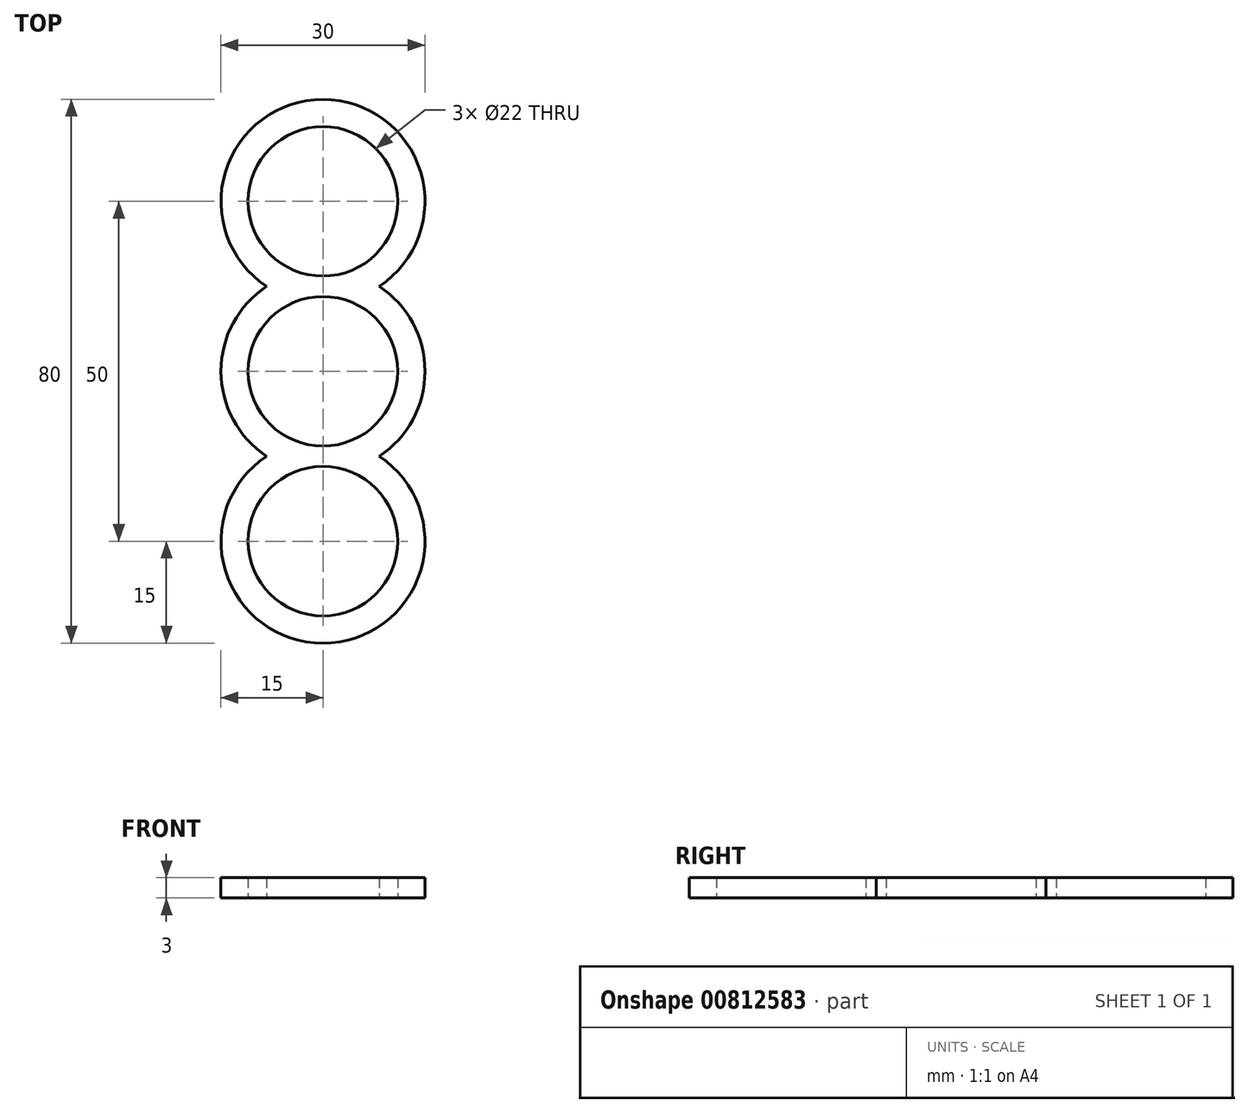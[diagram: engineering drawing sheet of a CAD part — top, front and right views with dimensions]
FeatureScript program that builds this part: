
annotation { "Feature Type Name" : "Feature", "Feature Type Description" : "" }
export const myFeature = defineFeature(function(context is Context, id is Id, definition is map)
    precondition{}
    {
        {
            var Q0;
            Q0=qCreatedBy(makeId("Top.planeOp"),FACE);
            var sketch = newSketch(context, id + "F0", { "sketchPlane" : qUnion([Q0])});
            skArc(sketch, "E0", {"start": v(11, 0) * mm, "mid": v(0, 11) * mm, "end": v(-11, 0) * mm});
            skArc(sketch, "E1", {"start": v(15, 0) * mm, "mid": v(13.22, 7.1) * mm, "end": v(8.3, 12.5) * mm});
            skLineSegment(sketch, "E2", {"start": v(0, 0) * mm, "end": v(0, 25) * mm});
            skCircle(sketch, "E3", {"center": v(0, 25) * mm, "radius": 11 * mm});
            skArc(sketch, "E4", {"start": v(8.3, 12.5) * mm, "mid": v(0, 40) * mm, "end": v(-8.3, 12.5) * mm});
            skArc(sketch, "E5.trimOffspring", {"start": v(-8.3, 12.5) * mm, "mid": v(-13.22, 7.1) * mm, "end": v(-15, 0) * mm});
            skArc(sketch, "E6.1.0", {"start": v(-8.3, -12.5) * mm, "mid": v(0, -40) * mm, "end": v(8.3, -12.5) * mm});
            skCircle(sketch, "E6.1.1", {"center": v(0, -25) * mm, "radius": 11 * mm});
            skArc(sketch, "E6.1.2", {"start": v(-15, 0) * mm, "mid": v(-13.22, -7.1) * mm, "end": v(-8.3, -12.5) * mm});
            skArc(sketch, "E6.1.3", {"start": v(-11, 0) * mm, "mid": v(0, -11) * mm, "end": v(11, 0) * mm});
            skArc(sketch, "E6.1.4", {"start": v(8.3, -12.5) * mm, "mid": v(13.22, -7.1) * mm, "end": v(15, 0) * mm});
            skSolve(sketch);
        }
        {
            var Q0;
            Q0 = qSketchRegion(id + "F0", true);
            extrude(context, id + "F1", {"entities" : qUnion([Q0]), "depth" : 3 * mm, "offsetDistance" : 25 * mm});
        }
    });
